# Revit family: Shades-Hunter_Douglas-RB500-Single_Heavy_Duty-Auto-55L_75L_Bracket-Pocket
name_source: partatom
category: Specialty Equipment
units: mm (PartAtom-declared; Revit-internal decimal feet)

## family parameters
Always vertical = Yes
Classification Number = 23.30.60.14
Cut with Voids When Loaded = No
Enable Cutting in Views = No
Maintain Annotation Orientation = No
Part Type = Normal
Room Calculation Point = No
Round Connector Dimension = Use Diameter
Shared = No
Work Plane-Based = No

## types (4) — shared parameters
Assembly Code = E2010300
CD_Bracket Depth = 0' - 5 1/4"
CD_Fabric Sizing Disclaimer = Designer to verify maximum fabric size with Manufacturer as the maximum fabric size is dependent on finished dimensions
CD_Finish = Fabric-Shade-Hunter_Douglas-5%-E_Screen-Charcoal_Cocoa
CD_Finish Frame = Metal-Aluminum-Hunter_Douglas-Anodized
CD_Finish Rail = Metal-Aluminum-Hunter_Douglas-Anodized
CD_Install Documentation = https://www.hunterdouglasarchitectural.com
CD_Microsite = https://microsite.caddetails.com
CD_Product Documentation Link = https://www.hunterdouglasarchitectural.com
CD_Product Name = RB 500 Roller Shade System
CD_Product Page URL = https://www.hunterdouglasarchitectural.com
CD_Screen Offset From Face = 0' - 0 29/32"
CD_Warranty = https://assets.hunterdouglasarchitectural.com
Default Elevation = 0' - 0"
Description = Heavy Duty Automatic Roller Shade
Manufacturer = Hunter Douglas Architectural
URL = https://www.hunterdouglasarchitectural.com

## per-type parameters (varying)
| type | 55L | 75L | CD_Bracket Height | CD_Bracket Offset | CD_Ceiling/Gypsum Pocket | CD_Ceiling/Gypsum Pocket 55L | CD_Ceiling/Gypsum Pocket 75L | CD_Roller CL Offset | CD_Surface Pocket | CD_Surface Pocket Calc | CD_Tile Pocket | CD_Tile Pocket Calc | Model | Type Comments |
| 55L Surface Pocket | Yes | No | 0' - 5 1/4" | 0' - 0 3/32" | No | No | No | 0' - 2 15/16" | Yes | Yes | No | No | Heavy Duty Automated 55L Bracket | Surface Pocket |
| 55L Tile Pocket | Yes | No | 0' - 5 1/4" | 0' - 0 3/32" | No | No | No | 0' - 2 15/16" | No | Yes | Yes | Yes | Heavy Duty Automated 55L Bracket | Tile Pocket |
| 55L Ceiling Pocket | Yes | No | 0' - 5 1/4" | 0' - 0 3/32" | Yes | Yes | No | 0' - 2 15/16" | No | No | No | No | Heavy Duty Automated 55L Bracket | Ceiling Pocket |
| 75L Gypsum Pocket | No | Yes | 0' - 6" | 0' - 0" | Yes | No | Yes | 0' - 3" | No | No | No | No | Heavy Duty Automated 75L Bracket | Gypsum Pocket |

## geometry (parser evidence)
native form markers: Sweep x3
no freeform markers — native parametric forms only
